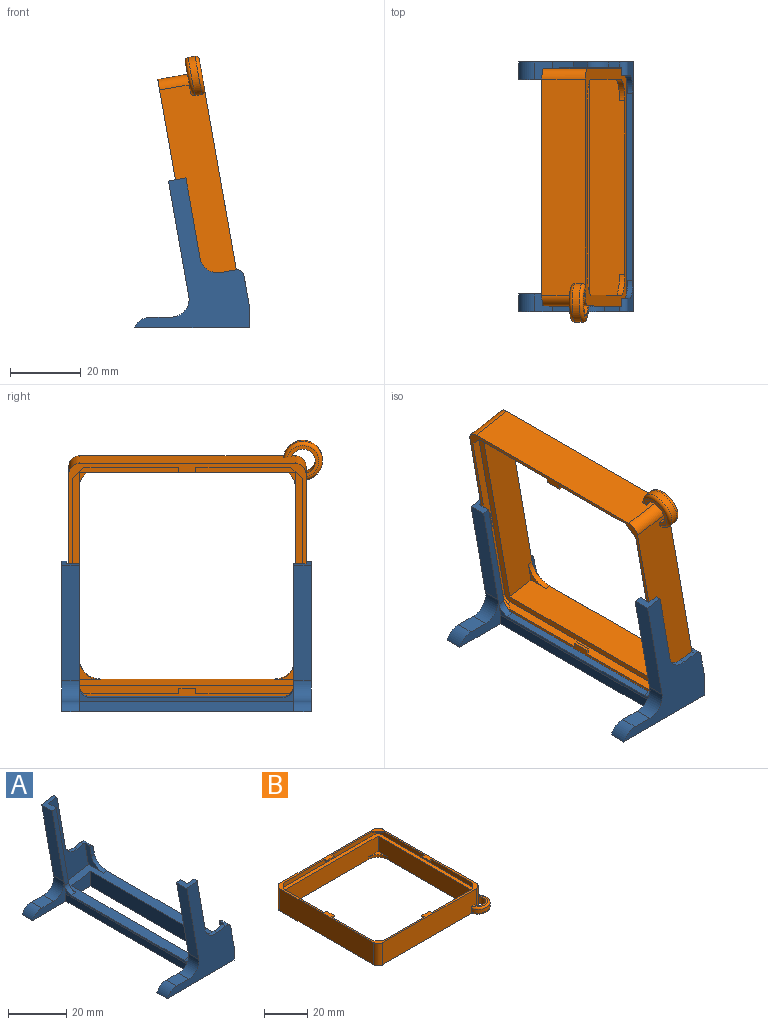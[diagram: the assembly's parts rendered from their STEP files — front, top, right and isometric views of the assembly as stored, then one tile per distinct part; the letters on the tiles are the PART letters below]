
ASSEMBLY  parts=2 mates=1
PART A: 46 faces, bbox 32.4x70.5x42.4 mm
  f0: plane 32.54x5.74mm, normal (-0.98,0,-0.17), area 165.2mm2, adj f14,f18,f26,f38
  f1: plane 60.5x3.94mm, normal (-0.98,0,-0.17), area 64.4mm2, adj f10,f23,f24,f29,f44,f45
  f2: plane 5.81x5mm, normal (0,0,1), area 29.1mm2, adj f18,f23,f30,f38
  f3: plane 70.5x32.44mm, normal (0,0,-1), area 738.8mm2, adj f12,f17,f18,f23,f24,f29,f30,f31
  f4: plane 9.79x7.3mm, normal (-0.98,0,-0.17), area 28.2mm2, adj f10,f21,f28,f33,f40
  f5: plane 4.26x1.5mm, normal (-0.17,0,0.98), area 6.5mm2, adj f17,f21,f33,f41
  f6: plane 70.5x8.86mm, normal (0.98,0,0.17), area 142mm2, adj f10,f12,f17,f18,f27,f28,f32,f33
  f7: plane 37.42x6.6mm, normal (0.98,0,0.17), area 134.9mm2, adj f10,f14,f20,f26,f45
  f8: plane 5x4.92mm, normal (-0.17,0,0.98), area 14.5mm2, adj f11,f15,f17,f21,f22,f25
  f9: plane 9.79x7.3mm, normal (-0.98,0,-0.17), area 28.2mm2, adj f10,f20,f27,f32,f39
  f10: plane 67.5x16.08mm, normal (-0.17,0,0.98), area 487.2mm2, adj f1,f4,f6,f7,f9,f11,f20,f21
  f11: plane 37.42x6.6mm, normal (0.98,0,0.17), area 134.9mm2, adj f8,f10,f21,f25,f44
  f12: plane 70.5x5.84mm, normal (1,0,0), area 411.4mm2, adj f3,f6,f17,f18
  f13: plane 3.28x1.5mm, normal (-0.17,0,0.98), area 5mm2, adj f18,f20,f32,f42
  f14: plane 5.91x5mm, normal (-0.17,0,0.98), area 16mm2, adj f0,f7,f18,f19,f20,f26
  f15: plane 32.54x5.74mm, normal (-0.98,0,-0.17), area 165.2mm2, adj f8,f17,f25,f43
  f16: plane 5.81x5mm, normal (0,0,1), area 29.1mm2, adj f17,f24,f31,f43
  f17: plane 42.28x32.44mm, normal (0,-1,0), area 448.4mm2, adj f3,f5,f6,f8,f12,f15,f16,f22
  f18: plane 42.45x32.44mm, normal (0,1,0), area 476.4mm2, adj f0,f2,f3,f6,f12,f13,f14,f19
  f19: plane 22.65x3.99mm, normal (0.98,0,0.17), area 34.5mm2, adj f14,f18,f20,f42
  f20: plane 38.12x19.23mm, normal (0,-1,0), area 245.7mm2, adj f7,f9,f10,f13,f14,f19,f32,f42
  f21: plane 37.94x19.23mm, normal (0,1,0), area 217.7mm2, adj f4,f5,f8,f10,f11,f22,f33,f41
  f22: plane 22.65x3.99mm, normal (0.98,0,0.17), area 34.5mm2, adj f8,f17,f21,f41
  f23: plane 16.36x8.87mm, normal (0,-1,0), area 53.2mm2, adj f1,f2,f3,f26,f29,f30,f38
  f24: plane 16.36x8.87mm, normal (0,1,0), area 53.2mm2, adj f1,f3,f16,f25,f29,f31,f43
  f25: plane 34.82x8.05mm, normal (0,1,0), area 70mm2, adj f8,f11,f15,f24,f44
  f26: plane 34.82x8.05mm, normal (0,-1,0), area 70mm2, adj f0,f7,f14,f23,f45
  f27: plane 4.86x2.33mm, normal (0,-1,0), area 6.7mm2, adj f6,f9,f32,f39
  f28: plane 4.86x2.33mm, normal (0,1,0), area 6.7mm2, adj f4,f6,f33,f40
  f29: plane 60.5x3mm, normal (-1,0,0), area 181.5mm2, adj f1,f3,f23,f24
  f30: cylinder r=5mm len=5mm, axis (0,-1,0), area 29mm2, adj f2,f3,f18,f23
  f31: cylinder r=5mm len=5mm, axis (0,-1,0), area 29mm2, adj f3,f16,f17,f24
  f32: cylinder r=2mm len=3.8mm, axis (0,1,0), area 10.8mm2, adj f6,f9,f13,f18,f20,f27
  f33: cylinder r=2mm len=3.8mm, axis (0,1,0), area 10.8mm2, adj f4,f5,f6,f17,f21,f28
  f34: plane 61.5x4.6mm, normal (1,0,0), area 283mm2, adj f3,f10,f35,f37
  f35: plane 9.08x6.2mm, normal (0,-1,0), area 49.1mm2, adj f3,f10,f34,f36
  f36: plane 61.5x6.2mm, normal (-1,0,0), area 381.5mm2, adj f3,f10,f35,f37
  f37: plane 9.08x6.2mm, normal (0,1,0), area 49.1mm2, adj f3,f10,f34,f36
  f38: cylinder r=5mm len=5.87mm, axis (0,1,0), area 43.6mm2, adj f0,f2,f18,f23
  f39: cylinder r=5mm len=5.18mm, axis (-0.98,0,-0.17), area 11.8mm2, adj f6,f9,f10,f27
  f40: cylinder r=5mm len=5.18mm, axis (0.98,0,0.17), area 11.8mm2, adj f4,f6,f10,f28
  f41: cylinder r=5mm len=5.79mm, axis (0,1,0), area 11.8mm2, adj f5,f17,f21,f22
  f42: cylinder r=5mm len=5.79mm, axis (0,1,0), area 11.8mm2, adj f13,f18,f19,f20
  f43: cylinder r=5mm len=5.87mm, axis (0,1,0), area 43.6mm2, adj f15,f16,f17,f24
  f44: cylinder r=3mm len=3.3mm, axis (0.98,0,0.17), area 9.4mm2, adj f1,f10,f11,f25
  f45: cylinder r=3mm len=3.3mm, axis (-0.98,0,-0.17), area 9.4mm2, adj f1,f7,f10,f26
PART B: 60 faces, bbox 72.1x72.1x12.5 mm
  f0: plane 61x2.4mm, normal (0,1,0), area 140.9mm2, adj f2,f3,f25,f26,f40,f41,f42,f43
  f1: plane 61x2.4mm, normal (1,0,0), area 140.9mm2, adj f3,f5,f25,f26,f36,f37,f40,f41
  f2: cylinder r=2mm len=2mm, axis (0,0,1), area 5.2mm2, adj f0,f15,f25,f43
  f3: cylinder r=2mm len=2mm, axis (0,0,-1), area 5.2mm2, adj f0,f1,f25,f41
  f4: cylinder r=2mm len=2mm, axis (0,0,-1), area 5.2mm2, adj f14,f15,f25,f39
  f5: cylinder r=2mm len=2mm, axis (0,0,1), area 5.2mm2, adj f1,f14,f25,f37
  f6: plane 6x6mm, normal (0,0,1), area 7.7mm2, adj f16,f19,f30
  f7: plane 6x6mm, normal (0,0,1), area 7.7mm2, adj f16,f17,f27
  f8: plane 6x6mm, normal (0,0,1), area 7.7mm2, adj f17,f18,f28
  f9: plane 70.62x70.62mm, normal (0,0,-1), area 808.3mm2, adj f10,f11,f12,f13,f16,f17,f18,f19
  f10: plane 61x12.5mm, normal (0,1,0), area 762.5mm2, adj f9,f21,f24,f26
  f11: plane 61x12.5mm, normal (-1,0,0), area 762.5mm2, adj f9,f21,f22,f26
  f12: plane 61x12.5mm, normal (0,-1,0), area 754.8mm2, adj f9,f22,f23,f26,f31,f32,f33,f34
  f13: plane 61x12.5mm, normal (1,0,0), area 754.8mm2, adj f9,f23,f24,f26,f31,f32,f33,f34
  f14: plane 61x2.4mm, normal (0,-1,0), area 140.9mm2, adj f4,f5,f25,f26,f36,f37,f38,f39
  f15: plane 61x2.4mm, normal (-1,0,0), area 140.9mm2, adj f2,f4,f25,f26,f38,f39,f42,f43
  f16: plane 61x10.1mm, normal (1,0,0), area 598.1mm2, adj f6,f7,f9,f17,f19,f25,f27,f30
  f17: plane 61x10.1mm, normal (0,1,0), area 598.1mm2, adj f7,f8,f9,f16,f18,f25,f27,f28
  f18: plane 61x10.1mm, normal (-1,0,0), area 598.1mm2, adj f8,f9,f17,f19,f20,f25,f28,f29
  f19: plane 61x10.1mm, normal (0,-1,0), area 598.1mm2, adj f6,f9,f16,f18,f20,f25,f29,f30
  f20: plane 6x6mm, normal (0,0,1), area 7.7mm2, adj f18,f19,f29
  f21: cylinder r=3mm len=12.5mm, axis (0,0,-1), area 58.9mm2, adj f9,f10,f11,f26
  f22: cylinder r=3mm len=12.5mm, axis (0,0,-1), area 58.9mm2, adj f9,f11,f12,f26
  f23: cylinder r=3mm len=12.5mm, axis (0,0,-1), area 58.9mm2, adj f9,f12,f13,f26
  f24: cylinder r=3mm len=12.5mm, axis (0,0,-1), area 58.9mm2, adj f9,f10,f13,f26
  f25: plane 65x65mm, normal (0,0,1), area 500.6mm2, adj f0,f1,f2,f3,f4,f5,f14,f15
  f26: plane 67x67mm, normal (0,0,1), area 306.8mm2, adj f0,f1,f10,f11,f12,f13,f14,f15
  f27: cylinder r=6mm len=6mm, axis (0,0,1), area 14.1mm2, adj f7,f9,f16,f17
  f28: cylinder r=6mm len=6mm, axis (0,0,1), area 14.1mm2, adj f8,f9,f17,f18
  f29: cylinder r=6mm len=6mm, axis (0,0,1), area 14.1mm2, adj f9,f18,f19,f20
  f30: cylinder r=6mm len=6mm, axis (0,0,1), area 14.1mm2, adj f6,f9,f16,f19
  f31: cylinder r=3.5mm len=6.89mm, axis (0,0,-1), area 58.9mm2, adj f9,f12,f13,f33
  f32: cylinder r=5.5mm len=10.93mm, axis (0,0,-1), area 48.3mm2, adj f12,f13,f34,f35
  f33: plane 8.91x8.91mm, normal (0,0,1), area 17.1mm2, adj f12,f13,f31,f35
  f34: torus R=4.5mm, axis (0,0,1), area 35.2mm2, adj f9,f12,f13,f32
  f35: torus R=4.5mm, axis (0,0,-1), area 35.2mm2, adj f12,f13,f32,f33
  f36: plane 3.29x3.29mm, normal (0.71,-0.71,0), area 3.5mm2, adj f1,f14,f26,f37
  f37: plane 3.29x3.29mm, normal (0,0,-1), area 4.6mm2, adj f1,f5,f14,f36
  f38: plane 3.29x3.29mm, normal (-0.71,-0.71,0), area 3.5mm2, adj f14,f15,f26,f39
  f39: plane 3.29x3.29mm, normal (0,0,-1), area 4.6mm2, adj f4,f14,f15,f38
  f40: plane 3.29x3.29mm, normal (0.71,0.71,0), area 3.5mm2, adj f0,f1,f26,f41
  f41: plane 3.29x3.29mm, normal (0,0,-1), area 4.6mm2, adj f0,f1,f3,f40
  f42: plane 3.29x3.29mm, normal (-0.71,0.71,0), area 3.5mm2, adj f0,f15,f26,f43
  f43: plane 3.29x3.29mm, normal (0,0,-1), area 4.6mm2, adj f0,f2,f15,f42
  f44: plane 1.5x0.75mm, normal (0,1,0), area 1.1mm2, adj f1,f26,f46,f47
  f45: plane 1.5x0.75mm, normal (0,-1,0), area 1.1mm2, adj f1,f26,f46,f47
  f46: plane 4.8x0.75mm, normal (1,0,0), area 3.6mm2, adj f26,f44,f45,f47
  f47: plane 4.8x1.5mm, normal (0,0,-1), area 7.2mm2, adj f1,f44,f45,f46
  f48: plane 1.5x0.75mm, normal (0,1,0), area 1.1mm2, adj f15,f26,f49,f51
  f49: plane 4.8x0.75mm, normal (-1,0,0), area 3.6mm2, adj f26,f48,f50,f51
  f50: plane 1.5x0.75mm, normal (0,-1,0), area 1.1mm2, adj f15,f26,f49,f51
  f51: plane 4.8x1.5mm, normal (0,0,-1), area 7.2mm2, adj f15,f48,f49,f50
  f52: plane 1.5x0.75mm, normal (-1,0,0), area 1.1mm2, adj f14,f26,f53,f55
  f53: plane 4.8x0.75mm, normal (0,-1,0), area 3.6mm2, adj f26,f52,f54,f55
  f54: plane 1.5x0.75mm, normal (1,0,0), area 1.1mm2, adj f14,f26,f53,f55
  f55: plane 4.8x1.5mm, normal (0,0,-1), area 7.2mm2, adj f14,f52,f53,f54
  f56: plane 4.8x0.75mm, normal (0,1,0), area 3.6mm2, adj f26,f57,f58,f59
  f57: plane 1.5x0.75mm, normal (-1,0,0), area 1.1mm2, adj f0,f26,f56,f59
  f58: plane 1.5x0.75mm, normal (1,0,0), area 1.1mm2, adj f0,f26,f56,f59
  f59: plane 4.8x1.5mm, normal (0,0,-1), area 7.2mm2, adj f0,f56,f57,f58
PLACE A t=(32.86,47.56,-145.62)mm
PLACE B rot(axis=(0,-1,0),100deg) t=(47.01,45.56,-142.36)mm
MATE slider A.f10 <-> B.f16  axis (-0.17,0,0.98) through (34.66,-21.44,-144.29)mm
